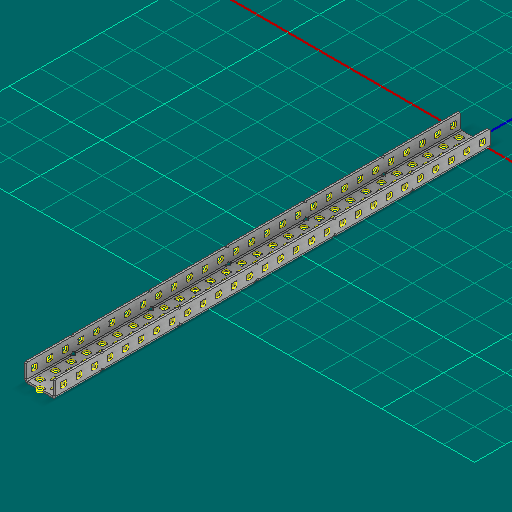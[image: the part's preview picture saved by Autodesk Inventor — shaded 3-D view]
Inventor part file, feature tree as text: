
AUTODESK INVENTOR PART (.ipt)
format: ipt  version: 2025 (Build 290162000, 162)  size: 2,258,432 bytes
history: native  units: in
note: dims shown in document units (in); Inventor stores cm internally (conversion verified against a paired STEP export)
features: other x286, sketch x5, sheet_metal_op x1
ambient origin geometry x8: Origin, YZ Plane, XZ Plane, XY Plane, X Axis, Y Axis, Z Axis, Center Point
bodies: Solid1 (feature_tree)
feature tree (292):
  other  "Alu C 1x2x1x28.ipt"
  other  "Solid1::Alu C 1x2x1x28.ipt"
  other  "TaggingFeature1"
  sketch  "Sketch1"  dims[d0=0.3937in]
  sketch  "Sketch2"  dims[d1=0.0625in]
  sketch  "Sketch3"
  other  "Flange Pattern Sketch"
  sketch  "Sketch9"
  sheet_metal_op  "Body Pattern Sketch"
  other  "Arc Length"
  sketch  "Sketch14"
  other  "Flange Pattern Plane"
  other  "Srf1"
  other  "Srf2"
  other  "Srf3"
  other  "Srf4"
  other  "Srf5"
  other  "Srf6"
  other  "Srf7"
  other  "Srf8"
  other  "Srf9"
  other  "Srf10"
  other  "Srf11"
  other  "Srf12"
  other  "Srf13"
  other  "Srf14"
  other  "Srf15"
  other  "Srf16"
  other  "Srf17"
  other  "Srf18"
  other  "Srf19"
  other  "Srf20"
  other  "Srf21"
  other  "Srf22"
  other  "Srf23"
  other  "Srf24"
  other  "Srf25"
  other  "Srf26"
  other  "Srf27"
  other  "Srf28"
  other  "Srf29"
  other  "Srf30"
  other  "Srf31"
  other  "Srf32"
  other  "Srf33"
  other  "Srf34"
  other  "Srf35"
  other  "Srf36"
  other  "Srf37"
  other  "Srf38"
  other  "Srf39"
  other  "Srf40"
  other  "Srf41"
  other  "Srf42"
  other  "Srf43"
  other  "Srf44"
  other  "Srf45"
  other  "Srf46"
  other  "Srf47"
  other  "Srf48"
  other  "Srf49"
  other  "Srf50"
  other  "Srf51"
  other  "Srf52"
  other  "Srf53"
  other  "Srf54"
  other  "Srf55"
  other  "Srf56"
  other  "Srf57"
  other  "Srf58"
  other  "Srf59"
  other  "Srf60"
  other  "Srf61"
  other  "Srf62"
  other  "Srf63"
  other  "Srf64"
  other  "Srf65"
  other  "Srf66"
  other  "Srf67"
  other  "Srf68"
  other  "Srf69"
  other  "Srf70"
  other  "Srf71"
  other  "Srf72"
  other  "Srf73"
  other  "Srf74"
  other  "Srf75"
  other  "Srf76"
  other  "Srf77"
  other  "Srf78"
  other  "Srf79"
  other  "Srf80"
  other  "Srf81"
  other  "Srf82"
  other  "Srf83"
  other  "Srf84"
  other  "Srf85"
  other  "Srf86"
  other  "Srf87"
  other  "Srf88"
  other  "Srf89"
  other  "Srf90"
  other  "Srf91"
  other  "Srf92"
  other  "Srf93"
  other  "Srf94"
  other  "Srf95"
  other  "Srf96"
  other  "Srf97"
  other  "Srf98"
  other  "Srf99"
  other  "Srf100"
  other  "Srf101"
  other  "Srf102"
  other  "Srf103"
  other  "Srf104"
  other  "Srf105"
  other  "Srf106"
  other  "Srf107"
  other  "Srf108"
  other  "Srf109"
  other  "Srf110"
  other  "Srf111"
  other  "Srf112"
  other  "Srf113"
  other  "Srf114"
  other  "Srf115"
  other  "Srf116"
  other  "Srf117"
  other  "Srf118"
  other  "Srf119"
  other  "Srf120"
  other  "Srf121"
  other  "Srf122"
  other  "Srf123"
  other  "Srf124"
  other  "Srf125"
  other  "Srf126"
  other  "Srf127"
  other  "Srf128"
  other  "Srf129"
  other  "Srf130"
  other  "Srf131"
  other  "Srf132"
  other  "Srf133"
  other  "Srf134"
  other  "Srf135"
  other  "Srf136"
  other  "Srf137"
  other  "Srf138"
  other  "Srf139"
  other  "Srf140"
  other  "Srf1::Derived"
  other  "Srf2::Derived"
  other  "Srf823::Derived"
  other  "Srf824::Derived"
  other  "Srf825::Derived"
  other  "Srf826::Derived"
  other  "Srf827::Derived"
  other  "Srf828::Derived"
  other  "Srf829::Derived"
  other  "Srf922::Derived"
  other  "Srf923::Derived"
  other  "Srf924::Derived"
  other  "Srf925::Derived"
  other  "Srf926::Derived"
  other  "Srf1143::Derived"
  other  "Srf1144::Derived"
  other  "Srf1145::Derived"
  other  "Srf1146::Derived"
  other  "Srf1147::Derived"
  other  "Srf1148::Derived"
  other  "Srf1149::Derived"
  other  "Srf1150::Derived"
  other  "Srf1151::Derived"
  other  "Srf1152::Derived"
  other  "Srf1153::Derived"
  other  "Srf1154::Derived"
  other  "Srf1155::Derived"
  other  "Srf1156::Derived"
  other  "Srf1157::Derived"
  other  "Srf1158::Derived"
  other  "Srf1159::Derived"
  other  "Srf1160::Derived"
  other  "Srf1161::Derived"
  other  "Srf1162::Derived"
  other  "Srf1163::Derived"
  other  "Srf1164::Derived"
  other  "Srf1165::Derived"
  other  "Srf1166::Derived"
  other  "Srf1167::Derived"
  other  "Srf1168::Derived"
  other  "Srf1169::Derived"
  other  "Srf1170::Derived"
  other  "Srf1171::Derived"
  other  "Srf1172::Derived"
  other  "Srf1173::Derived"
  other  "Srf1174::Derived"
  other  "Srf1175::Derived"
  other  "Srf1176::Derived"
  other  "Srf1177::Derived"
  other  "Srf1178::Derived"
  other  "Srf1179::Derived"
  other  "Srf1180::Derived"
  other  "Srf1181::Derived"
  other  "Srf1182::Derived"
  other  "Srf1183::Derived"
  other  "Srf1184::Derived"
  other  "Srf91::Derived"
  other  "Srf92::Derived"
  other  "Srf856::Derived"
  other  "Srf857::Derived"
  other  "Srf858::Derived"
  other  "Srf859::Derived"
  other  "Srf860::Derived"
  other  "Srf861::Derived"
  other  "Srf862::Derived"
  other  "Srf959::Derived"
  other  "Srf960::Derived"
  other  "Srf961::Derived"
  other  "Srf962::Derived"
  other  "Srf963::Derived"
  other  "Srf1199::Derived"
  other  "Srf1200::Derived"
  other  "Srf1201::Derived"
  other  "Srf1202::Derived"
  other  "Srf1203::Derived"
  other  "Srf1204::Derived"
  other  "Srf1205::Derived"
  other  "Srf1206::Derived"
  other  "Srf1207::Derived"
  other  "Srf1208::Derived"
  other  "Srf1209::Derived"
  other  "Srf1210::Derived"
  other  "Srf1211::Derived"
  other  "Srf1212::Derived"
  other  "Srf1213::Derived"
  other  "Srf1214::Derived"
  other  "Srf1215::Derived"
  other  "Srf1216::Derived"
  other  "Srf1217::Derived"
  other  "Srf1218::Derived"
  other  "Srf1219::Derived"
  other  "Srf1220::Derived"
  other  "Srf1221::Derived"
  other  "Srf1222::Derived"
  other  "Srf1223::Derived"
  other  "Srf1224::Derived"
  other  "Srf1225::Derived"
  other  "Srf1226::Derived"
  other  "Srf1227::Derived"
  other  "Srf1228::Derived"
  other  "Srf1229::Derived"
  other  "Srf1230::Derived"
  other  "Srf1231::Derived"
  other  "Srf1232::Derived"
  other  "Srf1233::Derived"
  other  "Srf1234::Derived"
  other  "Srf1235::Derived"
  other  "Srf1236::Derived"
  other  "Srf1237::Derived"
  other  "Srf1238::Derived"
  other  "Srf1239::Derived"
  other  "Srf1240::Derived"
  other  "Srf786::Derived"
  other  "Srf889::Derived"
  other  "Srf890::Derived"
  other  "Srf891::Derived"
  other  "Srf892::Derived"
  other  "Srf893::Derived"
  other  "Srf894::Derived"
  other  "Srf895::Derived"
  other  "Srf896::Derived"
  other  "Srf996::Derived"
  other  "Srf997::Derived"
  other  "Srf998::Derived"
  other  "Srf999::Derived"
  other  "Srf1000::Derived"
  other  "Srf1255::Derived"
  other  "Srf1256::Derived"
  other  "Srf1257::Derived"
  other  "Srf1258::Derived"
  other  "Srf1259::Derived"
  other  "Srf1260::Derived"
  other  "Srf1261::Derived"
  other  "Srf1262::Derived"
  other  "Srf1263::Derived"
  other  "Srf1264::Derived"
  other  "Srf1265::Derived"
  other  "Srf1266::Derived"
  other  "Srf1267::Derived"
  other  "Srf1268::Derived"
